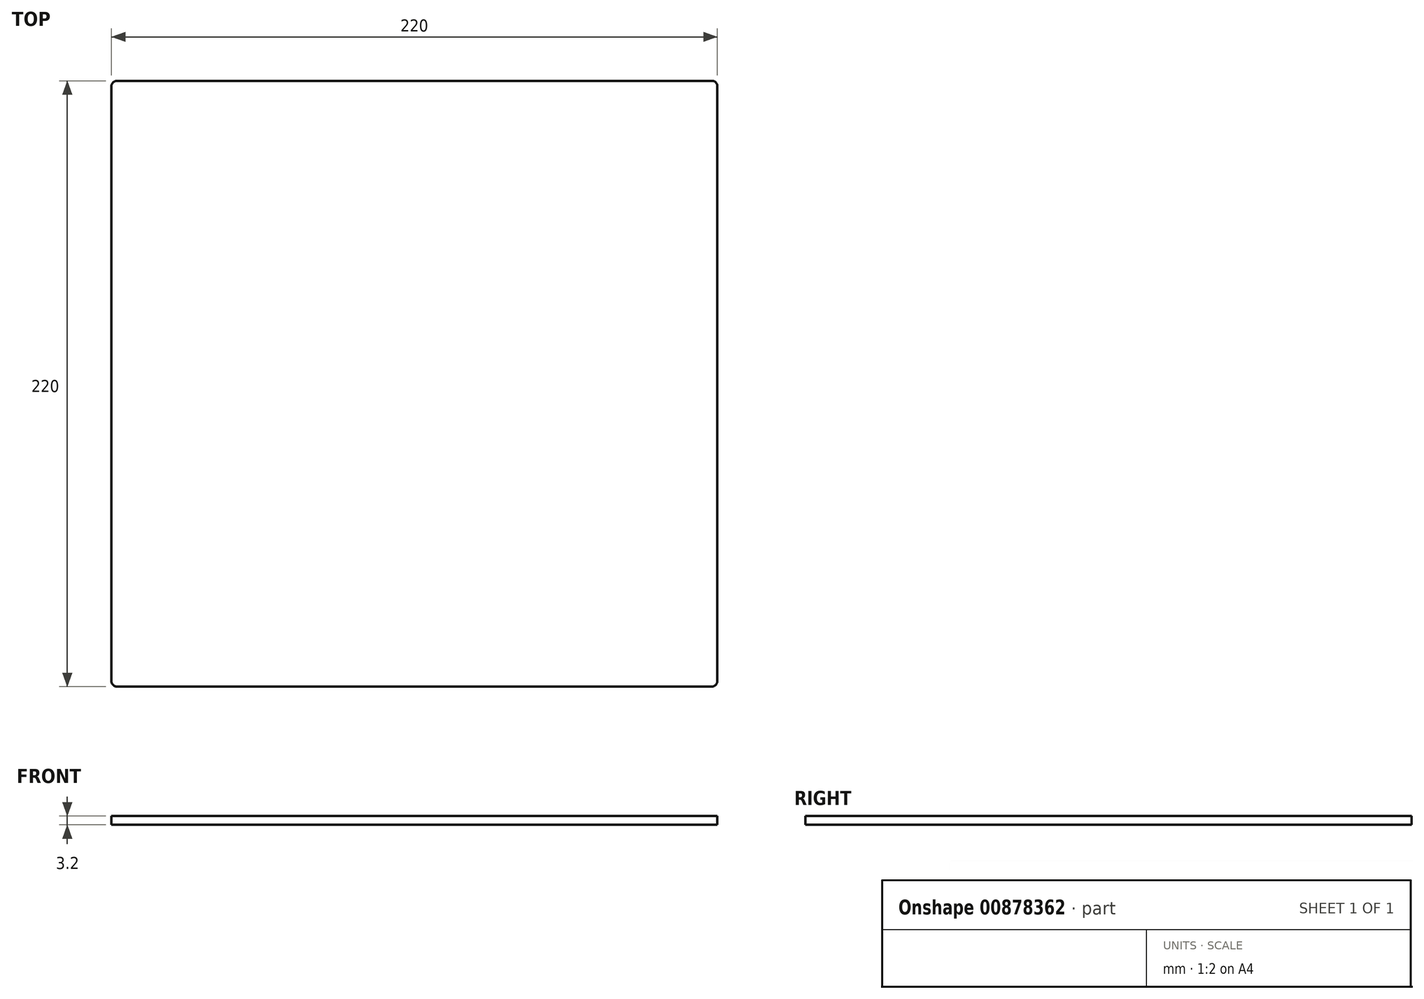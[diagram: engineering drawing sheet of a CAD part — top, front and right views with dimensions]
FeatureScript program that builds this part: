
annotation { "Feature Type Name" : "Feature", "Feature Type Description" : "" }
export const myFeature = defineFeature(function(context is Context, id is Id, definition is map)
    precondition{}
    {
        {
            var Q0;
            Q0=qCreatedBy(makeId("Top.planeOp"),FACE);
            var sketch = newSketch(context, id + "F0", { "sketchPlane" : qUnion([Q0])});
            skLineSegment(sketch, "E0.bottom", {"start": v(110, 110) * mm, "end": v(-110, 110) * mm});
            skLineSegment(sketch, "E0.top", {"start": v(110, -110) * mm, "end": v(-110, -110) * mm});
            skLineSegment(sketch, "E0.left", {"start": v(110, 110) * mm, "end": v(110, -110) * mm});
            skLineSegment(sketch, "E0.right", {"start": v(-110, 110) * mm, "end": v(-110, -110) * mm});
            skPoint(sketch, "E0.middle", {"position": v(0, 0) * mm});
            skSolve(sketch);
        }
        {
            var Q0;
            Q0=makeQuery(id+"F0.imprint","IMPRINT",FACE,{"disambiguationData":[TD([[makeQuery(id+"F0.imprint","IMPRINT",EDGE,{"derivedFrom":sQuery(id+"F0.wireOp",EDGE,"E0.bottom")}),1.0]])]});
            extrude(context, id + "F1", {"entities" : qUnion([Q0]), "depth" : 3.2 * mm, "offsetDistance" : 25 * mm});
        }
        {
            var Q0;
            Q0=makeQuery(id+"F1.opExtrude","SWEPT_EDGE",EDGE,{"disambiguationData":[OSD([sQuery(id+"F0.wireOp",EDGE,"E0.top"),sQuery(id+"F0.wireOp",EDGE,"E0.right")])]});
            var Q1;
            Q1=makeQuery(id+"F1.opExtrude","SWEPT_EDGE",EDGE,{"disambiguationData":[OSD([sQuery(id+"F0.wireOp",EDGE,"E0.top"),sQuery(id+"F0.wireOp",EDGE,"E0.left")])]});
            var Q2;
            Q2=makeQuery(id+"F1.opExtrude","SWEPT_EDGE",EDGE,{"disambiguationData":[OSD([sQuery(id+"F0.wireOp",EDGE,"E0.bottom"),sQuery(id+"F0.wireOp",EDGE,"E0.left")])]});
            var Q3;
            Q3=makeQuery(id+"F1.opExtrude","SWEPT_EDGE",EDGE,{"disambiguationData":[OSD([sQuery(id+"F0.wireOp",EDGE,"E0.bottom"),sQuery(id+"F0.wireOp",EDGE,"E0.right")])]});
            fillet(context, id + "F2", {"entities" : qUnion([Q0, Q1, Q2, Q3]), "tangentPropagation" : true, "radius" : 2 * mm, "defaultsChanged" : true, "vertexSettings" : [], "allowEdgeOverflow" : false});
        }
    });
